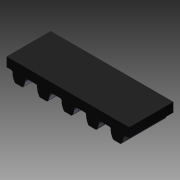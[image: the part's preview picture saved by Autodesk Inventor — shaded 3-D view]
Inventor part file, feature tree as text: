
AUTODESK INVENTOR PART (.ipt)
format: ipt  version: 2011 (Build 150239000, 239)  size: 137,216 bytes
history: native  units: in
note: dims shown in document units (in); Inventor stores cm internally (conversion verified against a paired STEP export)
features: extrude x1, sketch x1
ambient origin geometry x8: Origin, YZ Plane, XZ Plane, XY Plane, X Axis, Y Axis, Z Axis, Center Point
bodies: Solid1 (feature_tree)
feature tree (2):
  extrude  "Extrusion1"  Depth=0.1969in
  sketch  "Sketch1"  dims[d0=0.3543in d1=0.0in d2=0.1969in d3=0.15in d4=0.076in]
